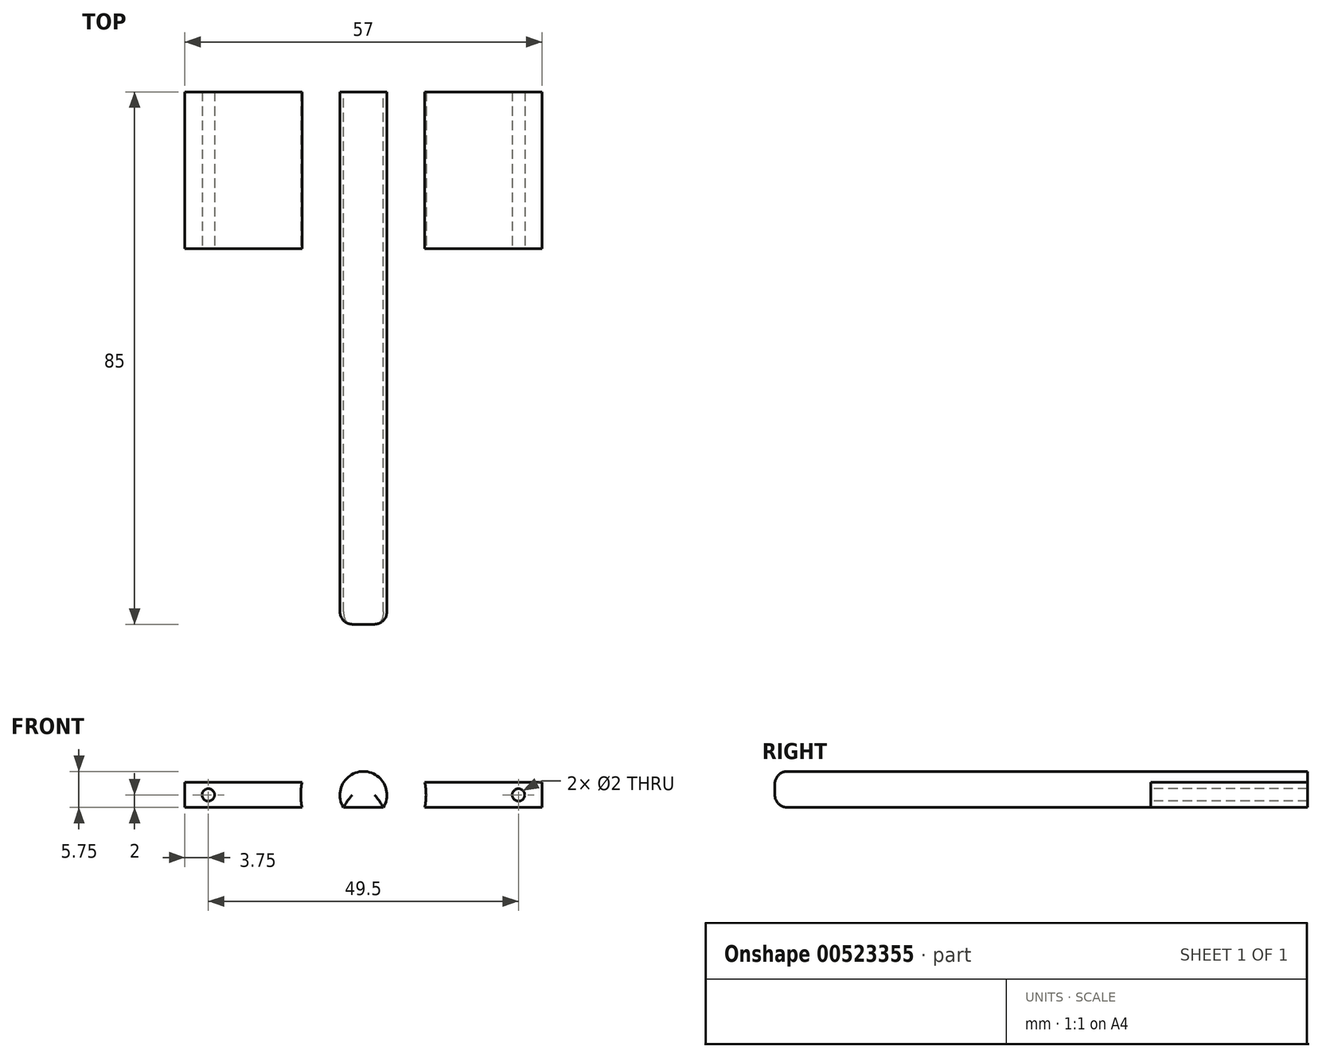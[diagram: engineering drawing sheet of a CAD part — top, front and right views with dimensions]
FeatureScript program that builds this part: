
annotation { "Feature Type Name" : "Feature", "Feature Type Description" : "" }
export const myFeature = defineFeature(function(context is Context, id is Id, definition is map)
    precondition{}
    {
        {
            var Q0;
            Q0=qCreatedBy(makeId("Front.planeOp"),FACE);
            var sketch = newSketch(context, id + "F0", { "sketchPlane" : qUnion([Q0])});
            skLineSegment(sketch, "E0", {"start": v(-3.17, 0) * mm, "end": v(3.17, 0) * mm});
            skArc(sketch, "E1", {"start": v(3.17, 0) * mm, "mid": v(0, 5.75) * mm, "end": v(-3.17, 0) * mm});
            skLineSegment(sketch, "E2.bottom", {"start": v(28.5, 4) * mm, "end": v(-28.5, 4) * mm});
            skLineSegment(sketch, "E2.top", {"start": v(28.5, 0) * mm, "end": v(-28.5, 0) * mm});
            skLineSegment(sketch, "E2.left", {"start": v(28.5, 4) * mm, "end": v(28.5, 0) * mm});
            skLineSegment(sketch, "E2.right", {"start": v(-28.5, 4) * mm, "end": v(-28.5, 0) * mm});
            skLineSegment(sketch, "E3", {"start": v(0, 4) * mm, "end": v(0, 0) * mm, "construction": true});
            skLineSegment(sketch, "E4", {"start": v(24.75, 2) * mm, "end": v(-24.75, 2) * mm, "construction": true});
            skCircle(sketch, "E5", {"center": v(-24.75, 2) * mm, "radius": 1 * mm});
            skCircle(sketch, "E6.MirrorC", {"center": v(24.75, 2) * mm, "radius": 1 * mm});
            skArc(sketch, "E7", {"start": v(9.8, 0) * mm, "mid": v(0, 12) * mm, "end": v(-9.8, 0) * mm});
            skSolve(sketch);
        }
        {
            var Q0;
            {var subQ0=sQuery(id+"F0.wireOp",EDGE,"E2.bottom");var subQ1=sQuery(id+"F0.wireOp",EDGE,"E1");var subQ2=makeQuery(id+"F0.imprint","INTERSECT",VERTEX,{"disambiguationData":[OD(0.0)],"derivedFrom":[subQ1,subQ0]});Q0=makeQuery(id+"F0.imprint","IMPRINT",FACE,{"disambiguationData":[TD([[makeQuery(id+"F0.imprint","IMPRINT",EDGE,{"disambiguationData":[TD([[subQ2,1.0]])],"derivedFrom":subQ1}),1.0]])]});}
            var Q1;
            {var subQ0=sQuery(id+"F0.wireOp",EDGE,"E0");Q1=makeQuery(id+"F0.imprint","IMPRINT",FACE,{"disambiguationData":[TD([[makeQuery(id+"F0.imprint","IMPRINT",EDGE,{"derivedFrom":subQ0}),1.0]])]});}
            extrude(context, id + "F1", {"entities" : qUnion([Q0, Q1]), "depth" : 80 * mm, "offsetDistance" : 25 * mm});
        }
        {
            var Q0;
            {var subQ0=sQuery(id+"F0.wireOp",EDGE,"E2.left");Q0=makeQuery(id+"F0.imprint","IMPRINT",FACE,{"disambiguationData":[TD([[makeQuery(id+"F0.imprint","IMPRINT",EDGE,{"derivedFrom":subQ0}),-1.0]])]});}
            var Q1;
            {var subQ3=sQuery(id+"F0.wireOp",EDGE,"E2.right");Q1=makeQuery(id+"F0.imprint","IMPRINT",FACE,{"disambiguationData":[TD([[makeQuery(id+"F0.imprint","IMPRINT",EDGE,{"derivedFrom":subQ3}),1.0]])]});}
            var Q2;
            {var subQ0=sQuery(id+"F0.wireOp",EDGE,"E0");Q2=makeQuery(id+"F0.imprint","IMPRINT",FACE,{"disambiguationData":[TD([[makeQuery(id+"F0.imprint","IMPRINT",EDGE,{"derivedFrom":subQ0}),1.0]])]});}
            var Q3;
            {var subQ3=sQuery(id+"F0.wireOp",EDGE,"E2.bottom");var subQ5=sQuery(id+"F0.wireOp",EDGE,"E7");var subQ6=makeQuery(id+"F0.imprint","INTERSECT",VERTEX,{"disambiguationData":[OD(1.0)],"derivedFrom":[subQ3,subQ5]});Q3=makeQuery(id+"F0.imprint","IMPRINT",FACE,{"disambiguationData":[TD([[makeQuery(id+"F0.imprint","IMPRINT",EDGE,{"disambiguationData":[TD([[subQ6,-1.0]])],"derivedFrom":subQ3}),1.0]])]});}
            var Q4;
            {var subQ3=sQuery(id+"F0.wireOp",EDGE,"E2.bottom");var subQ5=sQuery(id+"F0.wireOp",EDGE,"E7");var subQ6=makeQuery(id+"F0.imprint","INTERSECT",VERTEX,{"disambiguationData":[OD(0.0)],"derivedFrom":[subQ3,subQ5]});Q4=makeQuery(id+"F0.imprint","IMPRINT",FACE,{"disambiguationData":[TD([[makeQuery(id+"F0.imprint","IMPRINT",EDGE,{"disambiguationData":[TD([[subQ6,1.0]])],"derivedFrom":subQ3}),1.0]])]});}
            var Q5;
            {var subQ0=sQuery(id+"F0.wireOp",EDGE,"E2.bottom");var subQ1=sQuery(id+"F0.wireOp",EDGE,"E1");var subQ2=makeQuery(id+"F0.imprint","INTERSECT",VERTEX,{"disambiguationData":[OD(0.0)],"derivedFrom":[subQ1,subQ0]});Q5=makeQuery(id+"F0.imprint","IMPRINT",FACE,{"disambiguationData":[TD([[makeQuery(id+"F0.imprint","IMPRINT",EDGE,{"disambiguationData":[TD([[subQ2,1.0]])],"derivedFrom":subQ1}),1.0]])]});}
            extrude(context, id + "F2", {"entities" : qUnion([Q0, Q1, Q2, Q3, Q4, Q5]), "operationType" : NewBodyOperationType.ADD, "oppositeDirection" : true, "depth" : 5 * mm, "offsetDistance" : 25 * mm});
        }
        {
            var Q0;
            {var subQ3=sQuery(id+"F0.wireOp",EDGE,"E2.bottom");var subQ5=sQuery(id+"F0.wireOp",EDGE,"E7");var subQ6=makeQuery(id+"F0.imprint","INTERSECT",VERTEX,{"disambiguationData":[OD(1.0)],"derivedFrom":[subQ3,subQ5]});Q0=makeQuery(id+"F0.imprint","IMPRINT",FACE,{"disambiguationData":[TD([[makeQuery(id+"F0.imprint","IMPRINT",EDGE,{"disambiguationData":[TD([[subQ6,-1.0]])],"derivedFrom":subQ3}),1.0]])]});}
            var Q1;
            {var subQ3=sQuery(id+"F0.wireOp",EDGE,"E2.bottom");var subQ5=sQuery(id+"F0.wireOp",EDGE,"E7");var subQ6=makeQuery(id+"F0.imprint","INTERSECT",VERTEX,{"disambiguationData":[OD(0.0)],"derivedFrom":[subQ3,subQ5]});Q1=makeQuery(id+"F0.imprint","IMPRINT",FACE,{"disambiguationData":[TD([[makeQuery(id+"F0.imprint","IMPRINT",EDGE,{"disambiguationData":[TD([[subQ6,1.0]])],"derivedFrom":subQ3}),1.0]])]});}
            extrude(context, id + "F3", {"entities" : qUnion([Q0, Q1]), "operationType" : NewBodyOperationType.ADD, "depth" : 20 * mm, "offsetDistance" : 25 * mm});
        }
        {
            var Q0;
            Q0=makeQuery(id+"F1.opExtrude","CAP_FACE",FACE,{"disambiguationData":[OSD([sQuery(id+"F0.wireOp",EDGE,"E0"),sQuery(id+"F0.wireOp",EDGE,"E1")])],"isStart":false});
            var Q1;
            {var subQ0=sQuery(id+"F0.wireOp",EDGE,"E7");Q1=makeQuery(id+"F3.opExtrude","CAP_EDGE",EDGE,{"disambiguationData":[OSD([subQ0]),TDD([makeQuery(id+"F0.imprint","IMPRINT",EDGE,{"disambiguationData":[TD([[makeQuery(id+"F0.imprint","INTERSECT",VERTEX,{"disambiguationData":[OD(0.0)],"derivedFrom":[sQuery(id+"F0.wireOp",EDGE,"E2.bottom"),subQ0]}),-1.0]])],"derivedFrom":subQ0})])],"isStart":false});}
            var Q2;
            {var subQ0=sQuery(id+"F0.wireOp",EDGE,"E7");Q2=makeQuery(id+"F3.opExtrude","CAP_EDGE",EDGE,{"disambiguationData":[OSD([subQ0]),TDD([makeQuery(id+"F0.imprint","IMPRINT",EDGE,{"disambiguationData":[TD([[makeQuery(id+"F0.imprint","INTERSECT",VERTEX,{"disambiguationData":[OD(0.0)],"derivedFrom":[sQuery(id+"F0.wireOp",EDGE,"E2.top"),subQ0]}),-1.0]])],"derivedFrom":subQ0})])],"isStart":false});}
            var Q3;
            {var subQ0=sQuery(id+"F0.wireOp",EDGE,"E7");Q3=makeQuery(id+"F3.opExtrude","CAP_EDGE",EDGE,{"disambiguationData":[OSD([subQ0]),TDD([makeQuery(id+"F0.imprint","IMPRINT",EDGE,{"disambiguationData":[TD([[makeQuery(id+"F0.imprint","INTERSECT",VERTEX,{"disambiguationData":[OD(0.0)],"derivedFrom":[sQuery(id+"F0.wireOp",EDGE,"E2.bottom"),subQ0]}),-1.0]])],"derivedFrom":subQ0})])],"isStart":true});}
            var Q4;
            {var subQ0=sQuery(id+"F0.wireOp",EDGE,"E7");Q4=makeQuery(id+"F3.opExtrude","CAP_EDGE",EDGE,{"disambiguationData":[OSD([subQ0]),TDD([makeQuery(id+"F0.imprint","IMPRINT",EDGE,{"disambiguationData":[TD([[makeQuery(id+"F0.imprint","INTERSECT",VERTEX,{"disambiguationData":[OD(0.0)],"derivedFrom":[sQuery(id+"F0.wireOp",EDGE,"E2.top"),subQ0]}),-1.0]])],"derivedFrom":subQ0})])],"isStart":true});}
            var Q5;
            Q5=makeQuery(id+"F2.opExtrude","CAP_EDGE",EDGE,{"disambiguationData":[OSD([sQuery(id+"F0.wireOp",EDGE,"E2.right")])],"isStart":true});
            var Q6;
            Q6=makeQuery(id+"F2.opExtrude","CAP_EDGE",EDGE,{"disambiguationData":[OSD([sQuery(id+"F0.wireOp",EDGE,"E2.left")])],"isStart":true});
            fillet(context, id + "F4", {"entities" : qUnion([Q0, Q1, Q2, Q3, Q4, Q5, Q6]), "radius" : 2 * mm, "tangentPropagation" : true, "allowEdgeOverflow" : false});
        }
    });
